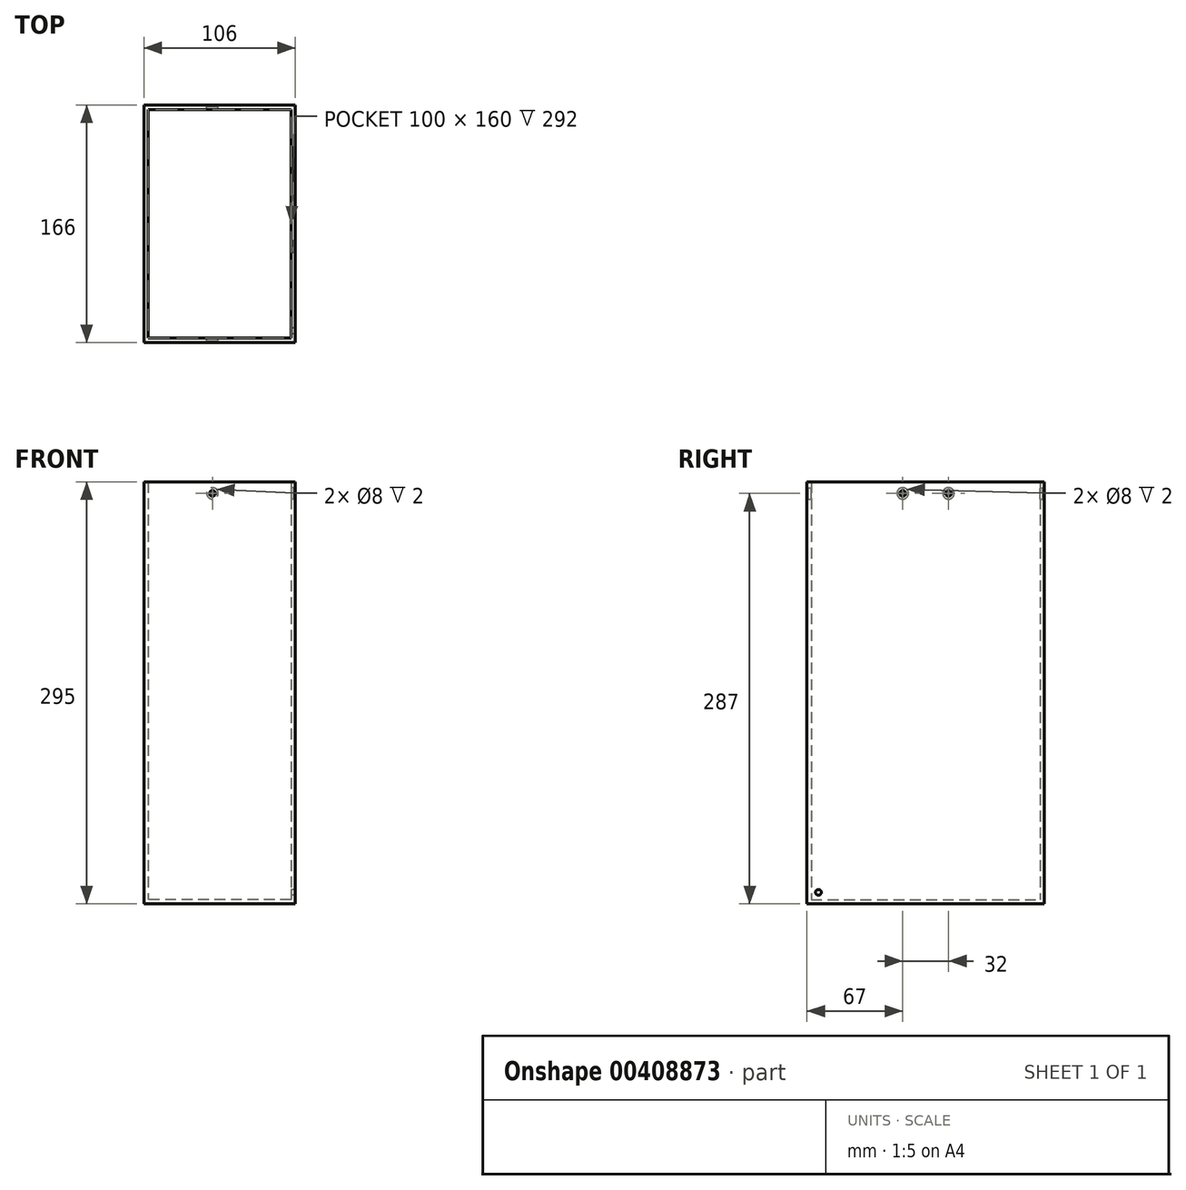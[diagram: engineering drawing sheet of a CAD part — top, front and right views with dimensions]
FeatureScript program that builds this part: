
annotation { "Feature Type Name" : "Feature", "Feature Type Description" : "" }
export const myFeature = defineFeature(function(context is Context, id is Id, definition is map)
    precondition{}
    {
        {
            var Q0;
            Q0=qCreatedBy(makeId("Top.planeOp"),FACE);
            var sketch = newSketch(context, id + "F0", { "sketchPlane" : qUnion([Q0])});
            skLineSegment(sketch, "E0.bottom", {"start": v(53, -83) * mm, "end": v(-53, -83) * mm});
            skLineSegment(sketch, "E0.top", {"start": v(53, 83) * mm, "end": v(-53, 83) * mm});
            skLineSegment(sketch, "E0.left", {"start": v(53, -83) * mm, "end": v(53, 83) * mm});
            skLineSegment(sketch, "E0.right", {"start": v(-53, -83) * mm, "end": v(-53, 83) * mm});
            skPoint(sketch, "E0.middle", {"position": v(0, 0) * mm});
            skSolve(sketch);
        }
        {
            var Q0;
            Q0=makeQuery(id+"F0.imprint","IMPRINT",FACE,{"disambiguationData":[TD([[makeQuery(id+"F0.imprint","IMPRINT",EDGE,{"derivedFrom":sQuery(id+"F0.wireOp",EDGE,"E0.bottom")}),-1.0]])]});
            extrude(context, id + "F1", {"entities" : qUnion([Q0]), "depth" : 295 * mm});
        }
        {
            var Q0;
            Q0=makeQuery(id+"F1.opExtrude","CAP_FACE",FACE,{"disambiguationData":[OSD([sQuery(id+"F0.wireOp",EDGE,"E0.bottom"),sQuery(id+"F0.wireOp",EDGE,"E0.top"),sQuery(id+"F0.wireOp",EDGE,"E0.left"),sQuery(id+"F0.wireOp",EDGE,"E0.right")])],"isStart":false});
            shell(context, id + "F2", {"entities" : qUnion([Q0]), "thickness" : 3 * mm});
        }
        {
            var Q0;
            Q0=qCreatedBy(makeId("Right.planeOp"),FACE);
            var sketch = newSketch(context, id + "F3", { "sketchPlane" : qUnion([Q0])});
            skCircle(sketch, "E1", {"center": v(-16, 287) * mm, "radius": 2 * mm});
            skCircle(sketch, "E2.1.0.0", {"center": v(16, 287) * mm, "radius": 2 * mm});
            skLineSegment(sketch, "E2.direction1", {"start": v(-16, 287) * mm, "end": v(16, 287) * mm, "construction": true});
            skCircle(sketch, "E3", {"center": v(-75, 8) * mm, "radius": 2 * mm});
            skSolve(sketch);
        }
        {
            var Q0;
            Q0 = qSketchRegion(id + "F3", true);
            extrude(context, id + "F4", {"entities" : qUnion([Q0]), "operationType" : NewBodyOperationType.REMOVE, "oppositeDirection" : true, "depth" : -150 * mm});
        }
        {
            var Q0;
            Q0=qCreatedBy(makeId("Front.planeOp"),FACE);
            var sketch = newSketch(context, id + "F5", { "sketchPlane" : qUnion([Q0])});
            skCircle(sketch, "E4", {"center": v(-5, 287) * mm, "radius": 2 * mm});
            skSolve(sketch);
        }
        {
            var Q0;
            Q0 = qSketchRegion(id + "F5", true);
            extrude(context, id + "F6", {"entities" : qUnion([Q0]), "operationType" : NewBodyOperationType.REMOVE, "depth" : 250 * mm, "symmetric" : true});
        }
        {
            var Q0;
            Q0=qCreatedBy(makeId("Right.planeOp"),FACE);
            var sketch = newSketch(context, id + "F7", { "sketchPlane" : qUnion([Q0])});
            skCircle(sketch, "E5", {"center": v(-16, 287) * mm, "radius": 4 * mm});
            skCircle(sketch, "E6.1.0.0", {"center": v(16, 287) * mm, "radius": 4 * mm});
            skLineSegment(sketch, "E6.direction1", {"start": v(-16, 287) * mm, "end": v(16, 287) * mm, "construction": true});
            skSolve(sketch);
        }
        {
            var Q0;
            Q0 = qSketchRegion(id + "F7", true);
            extrude(context, id + "F8", {"entities" : qUnion([Q0]), "operationType" : NewBodyOperationType.REMOVE, "oppositeDirection" : true, "depth" : -52 * mm});
        }
        {
            var Q0;
            Q0=qCreatedBy(makeId("Front.planeOp"),FACE);
            var sketch = newSketch(context, id + "F9", { "sketchPlane" : qUnion([Q0])});
            skCircle(sketch, "E7", {"center": v(-5, 287) * mm, "radius": 4 * mm});
            skSolve(sketch);
        }
        {
            var Q0;
            Q0 = qSketchRegion(id + "F9", true);
            extrude(context, id + "F10", {"entities" : qUnion([Q0]), "operationType" : NewBodyOperationType.REMOVE, "depth" : 164 * mm, "symmetric" : true});
        }
    });
